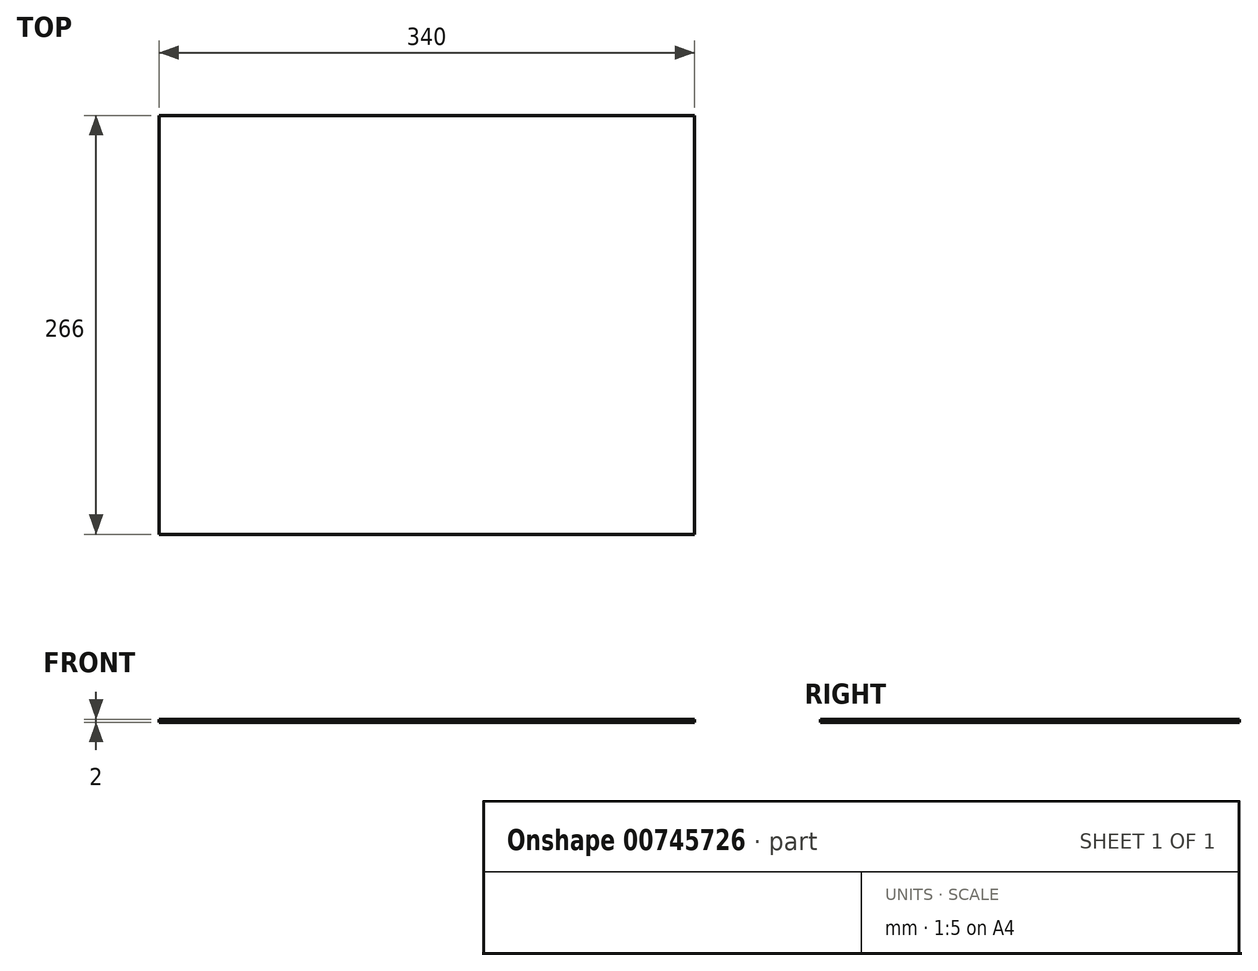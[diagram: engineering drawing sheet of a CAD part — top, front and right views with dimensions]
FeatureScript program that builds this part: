
annotation { "Feature Type Name" : "Feature", "Feature Type Description" : "" }
export const myFeature = defineFeature(function(context is Context, id is Id, definition is map)
    precondition{}
    {
        {
            var Q0;
            Q0=qCreatedBy(makeId("Top.planeOp"),FACE);
            var sketch = newSketch(context, id + "F0", { "sketchPlane" : qUnion([Q0])});
            skLineSegment(sketch, "E0.bottom", {"start": v(170, -133) * mm, "end": v(-170, -133) * mm});
            skLineSegment(sketch, "E0.top", {"start": v(170, 133) * mm, "end": v(-170, 133) * mm});
            skLineSegment(sketch, "E0.left", {"start": v(170, -133) * mm, "end": v(170, 133) * mm});
            skLineSegment(sketch, "E0.right", {"start": v(-170, -133) * mm, "end": v(-170, 133) * mm});
            skPoint(sketch, "E0.middle", {"position": v(0, 0) * mm});
            skSolve(sketch);
        }
        {
            var Q0;
            Q0=makeQuery(id+"F0.imprint","IMPRINT",FACE,{"disambiguationData":[TD([[makeQuery(id+"F0.imprint","IMPRINT",EDGE,{"derivedFrom":sQuery(id+"F0.wireOp",EDGE,"E0.bottom")}),-1.0]])]});
            extrude(context, id + "F1", {"entities" : qUnion([Q0]), "depth" : 2 * mm, "offsetDistance" : 25 * mm});
        }
    });
